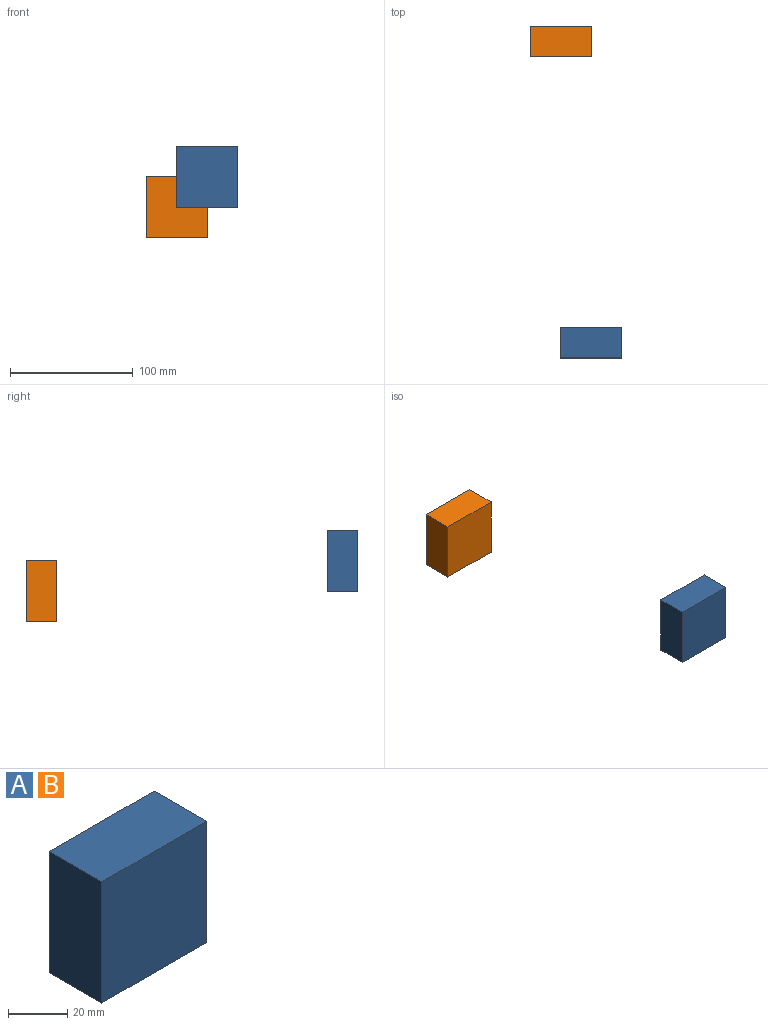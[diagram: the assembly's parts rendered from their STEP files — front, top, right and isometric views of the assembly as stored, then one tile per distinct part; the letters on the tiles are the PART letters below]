
ASSEMBLY  parts=2 mates=1
PART A: 6 faces, bbox 50x25x50 mm
  f0: plane 50x25mm, normal (0,0,1), area 1250mm2, adj f1,f3,f4,f5
  f1: plane 50x25mm, normal (-1,0,0), area 1250mm2, adj f0,f2,f4,f5
  f2: plane 50x25mm, normal (0,0,-1), area 1250mm2, adj f1,f3,f4,f5
  f3: plane 50x25mm, normal (1,0,0), area 1250mm2, adj f0,f2,f4,f5
  f4: plane 50x50mm, normal (0,-1,0), area 2500mm2, adj f0,f1,f2,f3
  f5: plane 50x50mm, normal (0,1,0), area 2500mm2, adj f0,f1,f2,f3
PART B: same geometry as A
PLACE A t=(-37.36,-262.26,63.39)mm
PLACE B t=(-62.36,-16.45,38.39)mm fixed
MATE slider B.f4 <-> A.f5  axis (0,-1,0) through (-62.36,-28.95,63.39)mm
